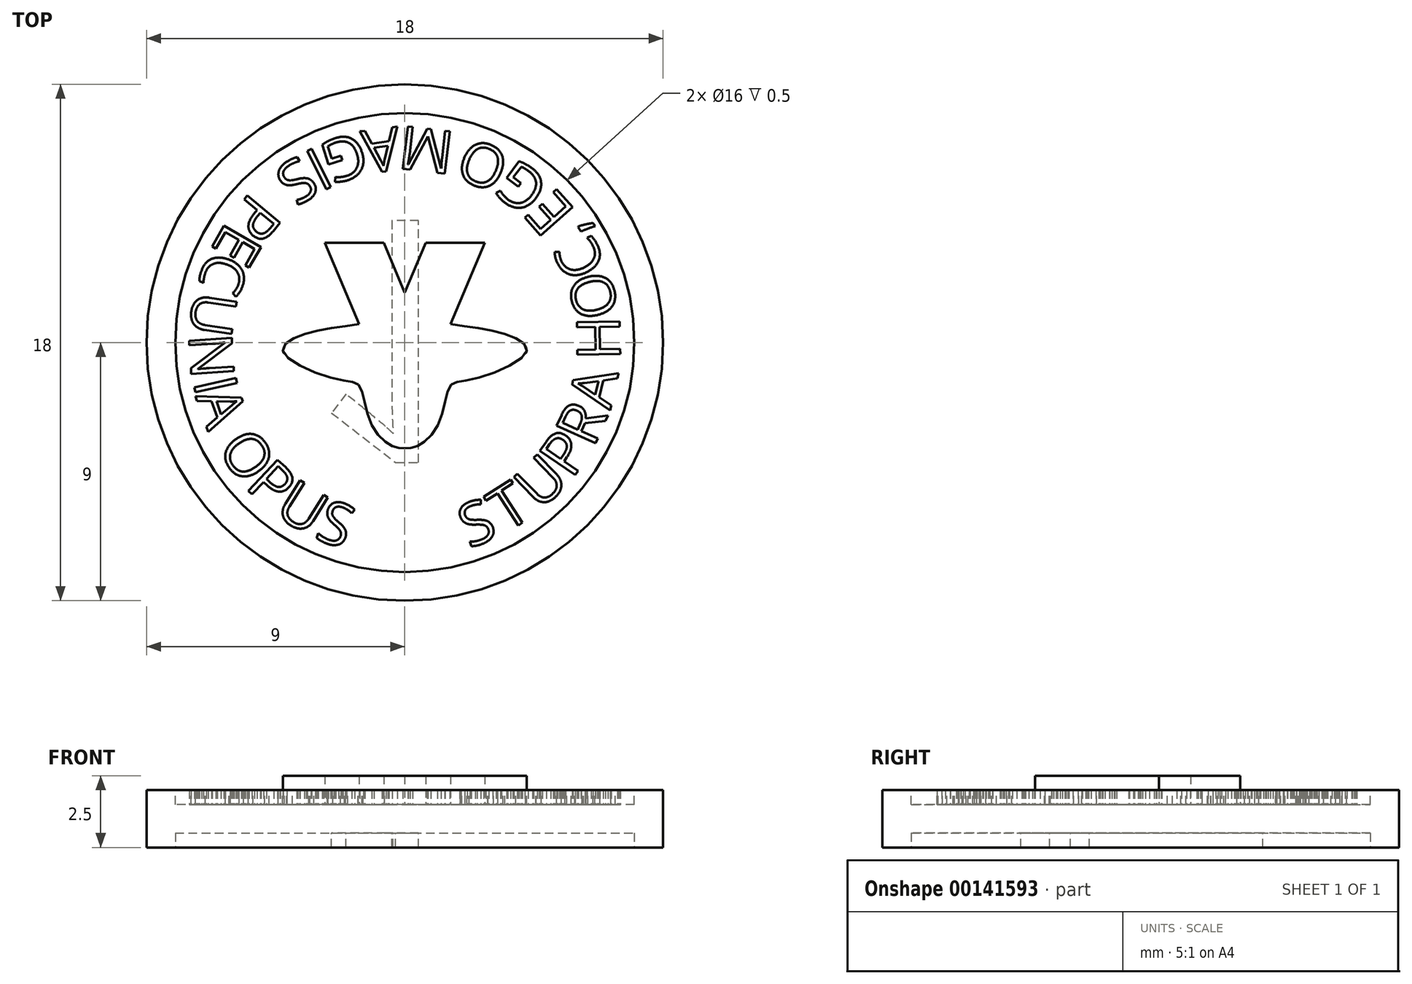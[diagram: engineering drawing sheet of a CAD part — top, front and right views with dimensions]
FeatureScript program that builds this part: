
annotation { "Feature Type Name" : "Feature", "Feature Type Description" : "" }
export const myFeature = defineFeature(function(context is Context, id is Id, definition is map)
    precondition{}
    {
        {
            assignVariable(context, id + "F0", {"name" : "ImpressionDepth", "anyValue" : 0.5});
        }
        {
            assignVariable(context, id + "F1", {"name" : "EmbossHeight", "anyValue" : 0.5});
        }
        {
            var Q0;
            Q0=qCreatedBy(makeId("Top.planeOp"),FACE);
            var sketch = newSketch(context, id + "F2", { "sketchPlane" : qUnion([Q0])});
            skCircle(sketch, "E0", {"center": v(0, 0) * mm, "radius": 9 * mm});
            skSolve(sketch);
        }
        {
            var Q0;
            Q0=qSketchRegion(id+"F2",true);
            extrude(context, id + "F3", {"entities" : qUnion([Q0]), "depth" : 2 * mm});
        }
        {
            var Q0;
            Q0=makeQuery(id+"F3.opExtrude","CAP_FACE",FACE,{"disambiguationData":[OSD([sQuery(id+"F2.wireOp",EDGE,"E0")])],"isStart":false});
            var sketch = newSketch(context, id + "F4", { "sketchPlane" : qUnion([Q0])});
            skCircle(sketch, "E1.0", {"center": v(0, 0) * mm, "radius": 8 * mm});
            skSolve(sketch);
        }
        {
            var Q0;
            Q0=qSketchRegion(id+"F4",true);
            extrude(context, id + "F5", {"entities" : qUnion([Q0]), "operationType" : NewBodyOperationType.REMOVE, "oppositeDirection" : true, "depth" : (getVariable(context, 'ImpressionDepth')) * mm});
        }
        {
            var Q0;
            Q0=makeQuery(id+"F3.opExtrude","CAP_FACE",FACE,{"disambiguationData":[OSD([sQuery(id+"F2.wireOp",EDGE,"E0")])],"isStart":true});
            var sketch = newSketch(context, id + "F6", { "sketchPlane" : qUnion([Q0])});
            skCircle(sketch, "E2.0", {"center": v(0, 0) * mm, "radius": 8 * mm});
            skSolve(sketch);
        }
        {
            var Q0;
            Q0=qSketchRegion(id+"F6",true);
            extrude(context, id + "F7", {"entities" : qUnion([Q0]), "operationType" : NewBodyOperationType.REMOVE, "oppositeDirection" : true, "depth" : (getVariable(context, 'ImpressionDepth')) * mm});
        }
        {
            var Q0;
            Q0=makeQuery(id+"F7.boolean.opBoolean","COPY",FACE,{"derivedFrom":makeQuery(id+"F7.opExtrude","CAP_FACE",FACE,{"disambiguationData":[OSD([sQuery(id+"F6.wireOp",EDGE,"E2.0")])],"isStart":false})});
            var sketch = newSketch(context, id + "F8", { "sketchPlane" : qUnion([Q0])});
            skText(sketch, "E3", { "text": "1", "fontName": "OpenSans-Regular.ttf"});
            skPoint(sketch, "E4", {"position": v(-1.2, 0) * mm});
            skLineSegment(sketch, "E5", {"start": v(-1.2, 0) * mm, "end": v(0, 0) * mm, "construction": true});
            const initialGuessF8  = {"E3": [-0.00364, -0.00425, 1, 0, 0.0085]};
            skSetInitialGuess(sketch, initialGuessF8);
            skSolve(sketch);
        }
        {
            var Q0;
            Q0 = qSketchRegion(id + "F8", true);
            extrude(context, id + "F9", {"entities" : qUnion([Q0]), "operationType" : NewBodyOperationType.ADD, "depth" : (getVariable(context, 'EmbossHeight')) * mm});
        }
        {
            var Q0;
            Q0=makeQuery(id+"F5.boolean.opBoolean","COPY",FACE,{"derivedFrom":makeQuery(id+"F5.opExtrude","CAP_FACE",FACE,{"disambiguationData":[OSD([sQuery(id+"F4.wireOp",EDGE,"E1.0")])],"isStart":false})});
            var sketch = newSketch(context, id + "F10", { "sketchPlane" : qUnion([Q0])});
            skLineSegment(sketch, "E6", {"start": v(0, -8) * mm, "end": v(0, 8) * mm, "construction": true});
            skLineSegment(sketch, "E7", {"start": v(0, 1.74) * mm, "end": v(-0.74, 3.47) * mm});
            skLineSegment(sketch, "E8", {"start": v(-0.74, 3.47) * mm, "end": v(-2.79, 3.47) * mm});
            skLineSegment(sketch, "E9", {"start": v(-2.79, 3.47) * mm, "end": v(-1.59, 0.64) * mm});
            skLineSegment(sketch, "E10.MirrorCS", {"start": v(0, 1.74) * mm, "end": v(0.74, 3.47) * mm});
            skLineSegment(sketch, "E11.MirrorCS", {"start": v(2.79, 3.47) * mm, "end": v(1.59, 0.64) * mm});
            skLineSegment(sketch, "E12.MirrorCS", {"start": v(0.74, 3.47) * mm, "end": v(2.79, 3.47) * mm});
            skFitSpline(sketch, "E13", {"points": [v(-1.59, 0.64) * mm, v(-3.63, 0.25) * mm, v(-4.24, -0.32) * mm, v(-2.25, -1.3) * mm, v(-1.59, -1.5) * mm, v(-1.19, -2.8) * mm, v(-0.45, -3.6) * mm, v(0, -3.68) * mm], "startDerivative": vector(-11.02, -1.68) * mm, "endDerivative": vector(4.81, 0) * mm});
            skFitSpline(sketch, "E14.MirrorCS", {"points": [v(1.59, 0.64) * mm, v(3.63, 0.25) * mm, v(4.24, -0.32) * mm, v(2.25, -1.3) * mm, v(1.59, -1.5) * mm, v(1.19, -2.8) * mm, v(0.45, -3.6) * mm, v(0, -3.68) * mm], "startDerivative": vector(11.02, -1.68) * mm, "endDerivative": vector(-4.81, 0) * mm});
            skSolve(sketch);
        }
        {
            var Q0;
            Q0 = qSketchRegion(id + "F10", true);
            extrude(context, id + "F11", {"entities" : qUnion([Q0]), "operationType" : NewBodyOperationType.ADD, "depth" : 1 * mm});
        }
        {
            var Q0;
            Q0=makeQuery(id+"F5.boolean.opBoolean","COPY",FACE,{"derivedFrom":makeQuery(id+"F5.opExtrude","CAP_FACE",FACE,{"disambiguationData":[OSD([sQuery(id+"F4.wireOp",EDGE,"E1.0")])],"isStart":false})});
            var sketch = newSketch(context, id + "F12", { "sketchPlane" : qUnion([Q0])});
            skCircle(sketch, "E15.0", {"center": v(0, 0) * mm, "radius": 7.5 * mm, "construction": true});
            skText(sketch, "E16", { "text": "S", "fontName": "OpenSans-Regular.ttf"});
            skText(sketch, "E17", { "text": "I", "fontName": "OpenSans-Regular.ttf"});
            skText(sketch, "E18", { "text": "G", "fontName": "OpenSans-Regular.ttf"});
            skText(sketch, "E19", { "text": "A", "fontName": "OpenSans-Regular.ttf"});
            skLineSegment(sketch, "E20", {"start": v(0, 0) * mm, "end": v(0, 7.5) * mm, "construction": true});
            skText(sketch, "E21", { "text": "M", "fontName": "OpenSans-Regular.ttf"});
            skText(sketch, "E22", { "text": "P", "fontName": "OpenSans-Regular.ttf"});
            skText(sketch, "E23", { "text": "E", "fontName": "OpenSans-Regular.ttf"});
            skText(sketch, "E24", { "text": "C", "fontName": "OpenSans-Regular.ttf"});
            skText(sketch, "E25", { "text": "U", "fontName": "OpenSans-Regular.ttf"});
            skText(sketch, "E26", { "text": "N", "fontName": "OpenSans-Regular.ttf"});
            skText(sketch, "E27", { "text": "I", "fontName": "OpenSans-Regular.ttf"});
            skText(sketch, "E28", { "text": "A", "fontName": "OpenSans-Regular.ttf"});
            skPoint(sketch, "E29", {"position": v(-6.14, 2.87) * mm});
            skText(sketch, "E30", { "text": "O", "fontName": "OpenSans-Regular.ttf"});
            skText(sketch, "E31", { "text": "P", "fontName": "OpenSans-Regular.ttf"});
            skText(sketch, "E32", { "text": "U", "fontName": "OpenSans-Regular.ttf"});
            skText(sketch, "E33", { "text": "S", "fontName": "OpenSans-Regular.ttf"});
            skText(sketch, "E34", { "text": "S", "fontName": "OpenSans-Regular.ttf"});
            skText(sketch, "E35", { "text": "T", "fontName": "OpenSans-Regular.ttf"});
            skText(sketch, "E36", { "text": "U", "fontName": "OpenSans-Regular.ttf"});
            skText(sketch, "E37", { "text": "P", "fontName": "OpenSans-Regular.ttf"});
            skText(sketch, "E38", { "text": "R", "fontName": "OpenSans-Regular.ttf"});
            skText(sketch, "E39", { "text": "A", "fontName": "OpenSans-Regular.ttf"});
            skText(sketch, "E40", { "text": "H", "fontName": "OpenSans-Regular.ttf"});
            skText(sketch, "E41", { "text": "O", "fontName": "OpenSans-Regular.ttf"});
            skText(sketch, "E42", { "text": "C", "fontName": "OpenSans-Regular.ttf"});
            skText(sketch, "E43", { "text": ",", "fontName": "OpenSans-Regular.ttf"});
            skText(sketch, "E44", { "text": "E", "fontName": "OpenSans-Regular.ttf"});
            skText(sketch, "E45", { "text": "G", "fontName": "OpenSans-Regular.ttf"});
            skText(sketch, "E46", { "text": "O", "fontName": "OpenSans-Regular.ttf"});
            const initialGuessF12  = {"E16": [-0.00369, 0.00656, -0.83068, -0.55674, 0.0015], "E17": [-0.00292, 0.00525, 0.89418, 0.44771, 0.0015], "E18": [-0.0016, 0.00737, -0.9513, -0.30828, 0.0015], "E19": [-0.00026, 0.00753, -0.99144, -0.13053, 0.0015], "E21": [0.00177, 0.00734, -0.9933, 0.1156, 0.0015], "E22": [-0.00536, 0.00528, -0.63874, -0.76943, 0.0015], "E23": [-0.0062, 0.00425, -0.49963, -0.86624, 0.0015], "E24": [-0.00678, 0.00327, -0.34943, -0.93696, 0.0015], "E25": [-0.00731, 0.00183, -0.14699, -0.98914, 0.0015], "E26": [-0.00753, 0.00027, 0.06408, -0.99794, 0.0015], "E27": [-0.00738, -0.00136, 0.21531, -0.97655, 0.0015], "E28": [-0.0073, -0.00187, 0.34016, -0.94037, 0.0015], "E30": [-0.00657, -0.0037, 0.58166, -0.81343, 0.0015], "E31": [-0.0056, -0.00503, 0.72875, -0.68478, 0.0015], "E32": [-0.0046, -0.00596, 0.84697, -0.53165, 0.0015], "E33": [-0.00319, -0.00681, 0.93625, -0.35134, 0.0015], "E34": [0.00224, -0.00718, 0.9286, 0.37107, 0.0015], "E35": [0.00354, -0.00664, 0.83977, 0.54294, 0.0015], "E36": [0.0047, -0.00589, 0.7171, 0.69698, 0.0015], "E37": [0.00582, -0.00478, 0.56662, 0.82398, 0.0015], "E38": [0.00657, -0.00369, 0.407, 0.91343, 0.0015], "E39": [0.00716, -0.00236, 0.22024, 0.97545, 0.0015], "E40": [0.00751, -0.0006, -0.0188, 0.99982, 0.0015], "E41": [0.00748, 0.00102, -0.24105, 0.97051, 0.0015], "E42": [0.00705, 0.00266, -0.43832, 0.89882, 0.0015], "E43": [0.00644, 0.00386, -0.54254, 0.84003, 0.0015], "E44": [0.00598, 0.00457, -0.66727, 0.74481, 0.0015], "E45": [0.00511, 0.00554, -0.7985, 0.602, 0.0015], "E46": [0.00375, 0.00654, -0.9161, 0.40096, 0.0015]};
            skSetInitialGuess(sketch, initialGuessF12);
            skSolve(sketch);
        }
        {
            var Q0;
            Q0 = qSketchRegion(id + "F12", true);
            extrude(context, id + "F13", {"entities" : qUnion([Q0]), "operationType" : NewBodyOperationType.ADD, "depth" : (getVariable(context, 'EmbossHeight')) * mm});
        }
    });
